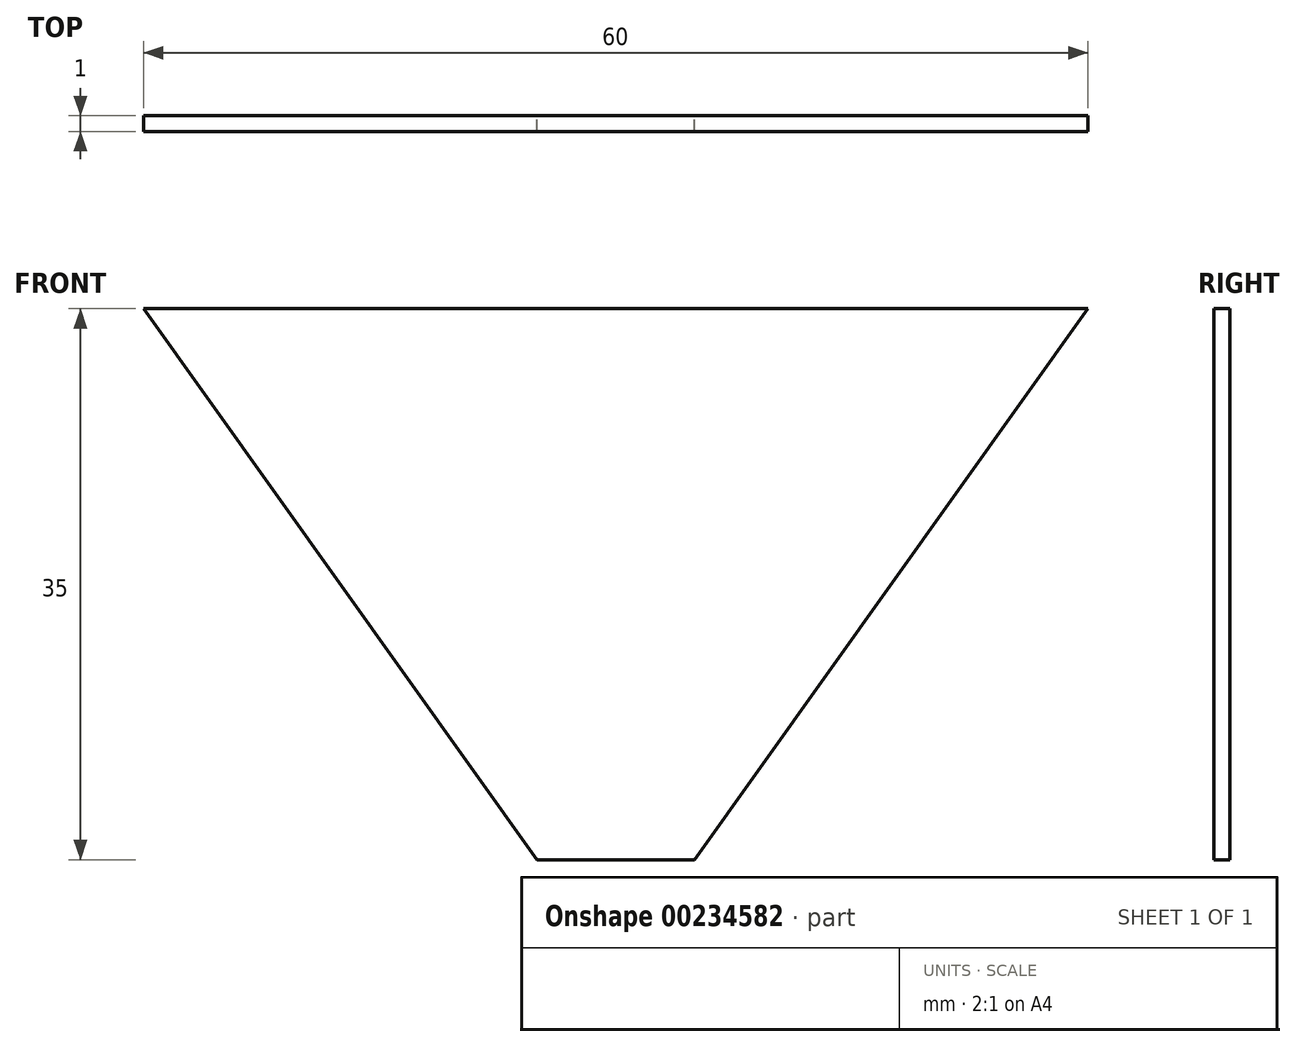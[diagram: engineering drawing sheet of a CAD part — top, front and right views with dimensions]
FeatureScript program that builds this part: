
annotation { "Feature Type Name" : "Feature", "Feature Type Description" : "" }
export const myFeature = defineFeature(function(context is Context, id is Id, definition is map)
    precondition{}
    {
        {
            var Q0;
            Q0=qCreatedBy(makeId("Front.planeOp"),FACE);
            var sketch = newSketch(context, id + "F0", { "sketchPlane" : qUnion([Q0])});
            skLineSegment(sketch, "E0", {"start": v(0, 0) * mm, "end": v(10, 0) * mm});
            skLineSegment(sketch, "E1", {"start": v(10, 0) * mm, "end": v(35, 35) * mm});
            skLineSegment(sketch, "E2", {"start": v(35, 35) * mm, "end": v(-25, 35) * mm});
            skLineSegment(sketch, "E3", {"start": v(-25, 35) * mm, "end": v(0, 0) * mm});
            skSolve(sketch);
        }
        {
            var Q0;
            Q0 = qSketchRegion(id + "F0", true);
            extrude(context, id + "F1", {"entities" : qUnion([Q0]), "depth" : 1 * mm});
        }
    });
